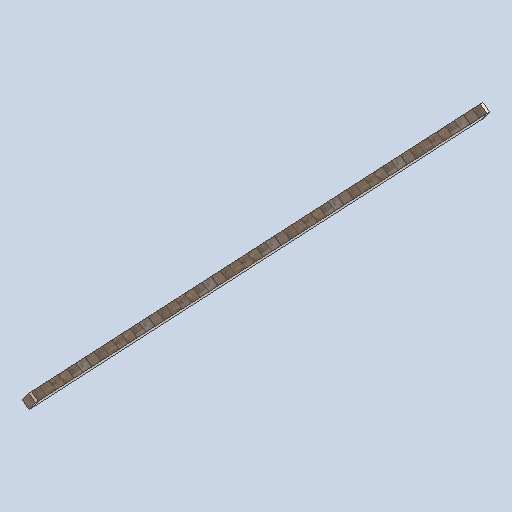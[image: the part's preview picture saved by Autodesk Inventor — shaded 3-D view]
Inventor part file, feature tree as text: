
AUTODESK INVENTOR PART (.ipt)
format: ipt  version: 2024.2 (Build 282272000, 272)  size: 133,632 bytes
history: native  units: in
note: dims shown in document units (in); Inventor stores cm internally (conversion verified against a paired STEP export)
features: sketch x4, other x3, plane x2
ambient origin geometry x8: Origin, YZ Plane, XZ Plane, XY Plane, X Axis, Y Axis, Z Axis, Center Point
bodies: Solid1 (feature_tree)
feature tree (9):
  other  "support_beam_segment_0104.ipt"
  other  "Solid1::support_beam_segment_0104.ipt"
  other  "TaggingFeature1"
  sketch  "Sketch1"  dims[d0=0.3937in]
  sketch  "Sketch2"
  sketch  "Sketch3"
  sketch  "Sketch4"
  plane  "Work Plane1"
  plane  "Work Plane2"
